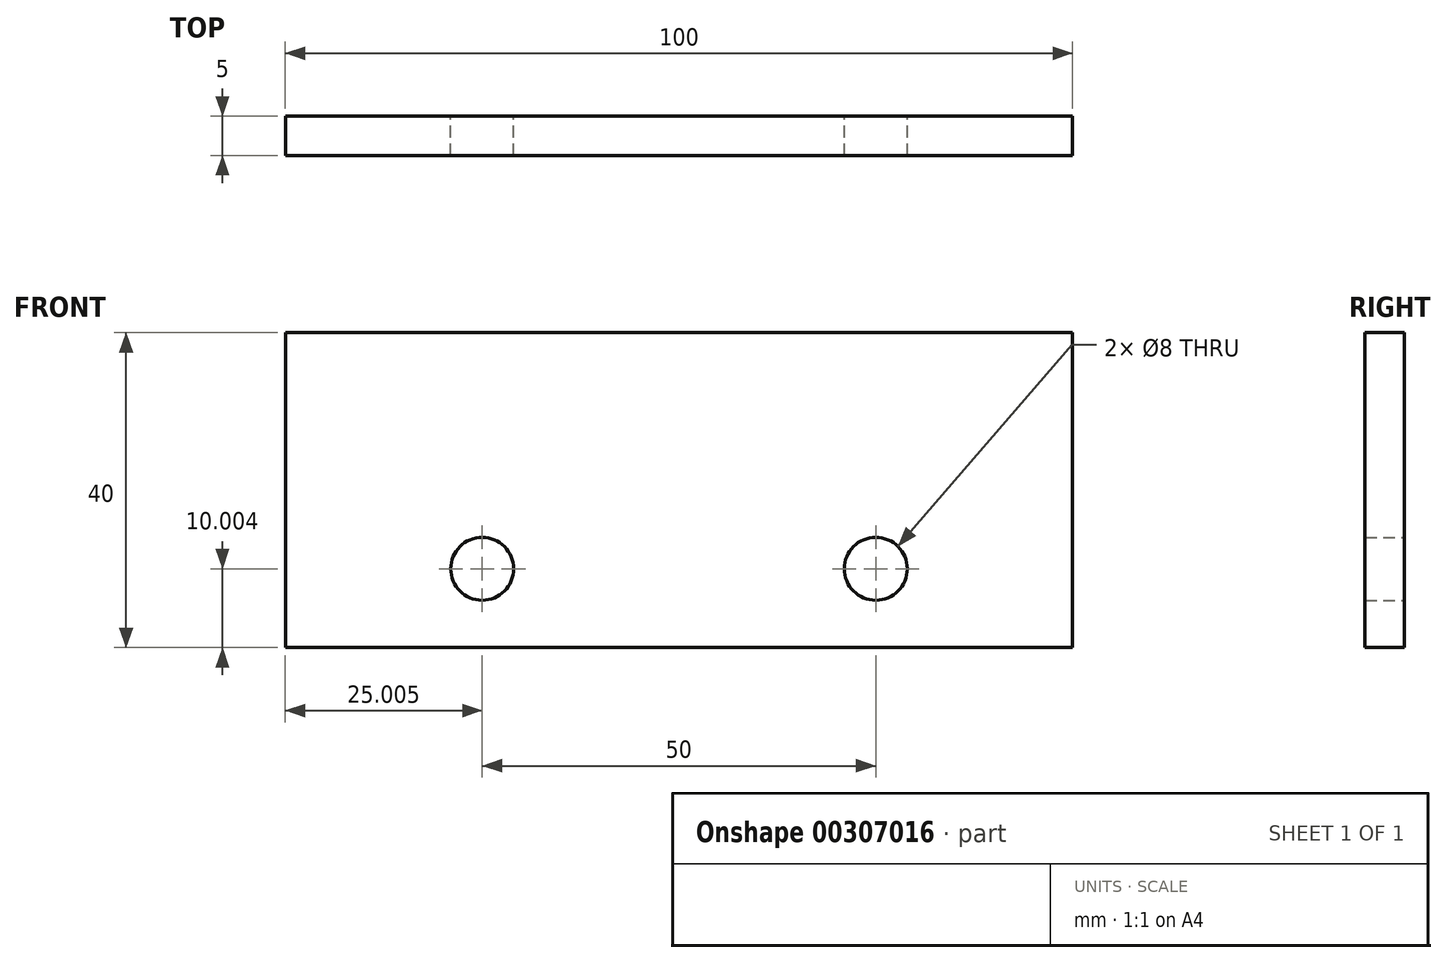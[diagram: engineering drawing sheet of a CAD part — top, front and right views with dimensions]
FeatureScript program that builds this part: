
annotation { "Feature Type Name" : "Feature", "Feature Type Description" : "" }
export const myFeature = defineFeature(function(context is Context, id is Id, definition is map)
    precondition{}
    {
        {
            var Q0;
            Q0=qCreatedBy(makeId("Front.planeOp"),FACE);
            var sketch = newSketch(context, id + "F0", { "sketchPlane" : qUnion([Q0])});
            skLineSegment(sketch, "E0.bottom", {"start": v(-57.19, 28.23) * mm, "end": v(42.81, 28.23) * mm});
            skLineSegment(sketch, "E0.top", {"start": v(-57.19, -11.77) * mm, "end": v(42.81, -11.77) * mm});
            skLineSegment(sketch, "E0.left", {"start": v(-57.19, 28.23) * mm, "end": v(-57.19, -11.77) * mm});
            skLineSegment(sketch, "E0.right", {"start": v(42.81, 28.23) * mm, "end": v(42.81, -11.77) * mm});
            skCircle(sketch, "E1", {"center": v(-32.19, -1.77) * mm, "radius": 4 * mm});
            skCircle(sketch, "E2", {"center": v(17.81, -1.77) * mm, "radius": 4 * mm});
            skSolve(sketch);
        }
        {
            var Q0;
            Q0 = qSketchRegion(id + "F0", true);
            extrude(context, id + "F1", {"entities" : qUnion([Q0]), "depth" : 5 * mm});
        }
    });
